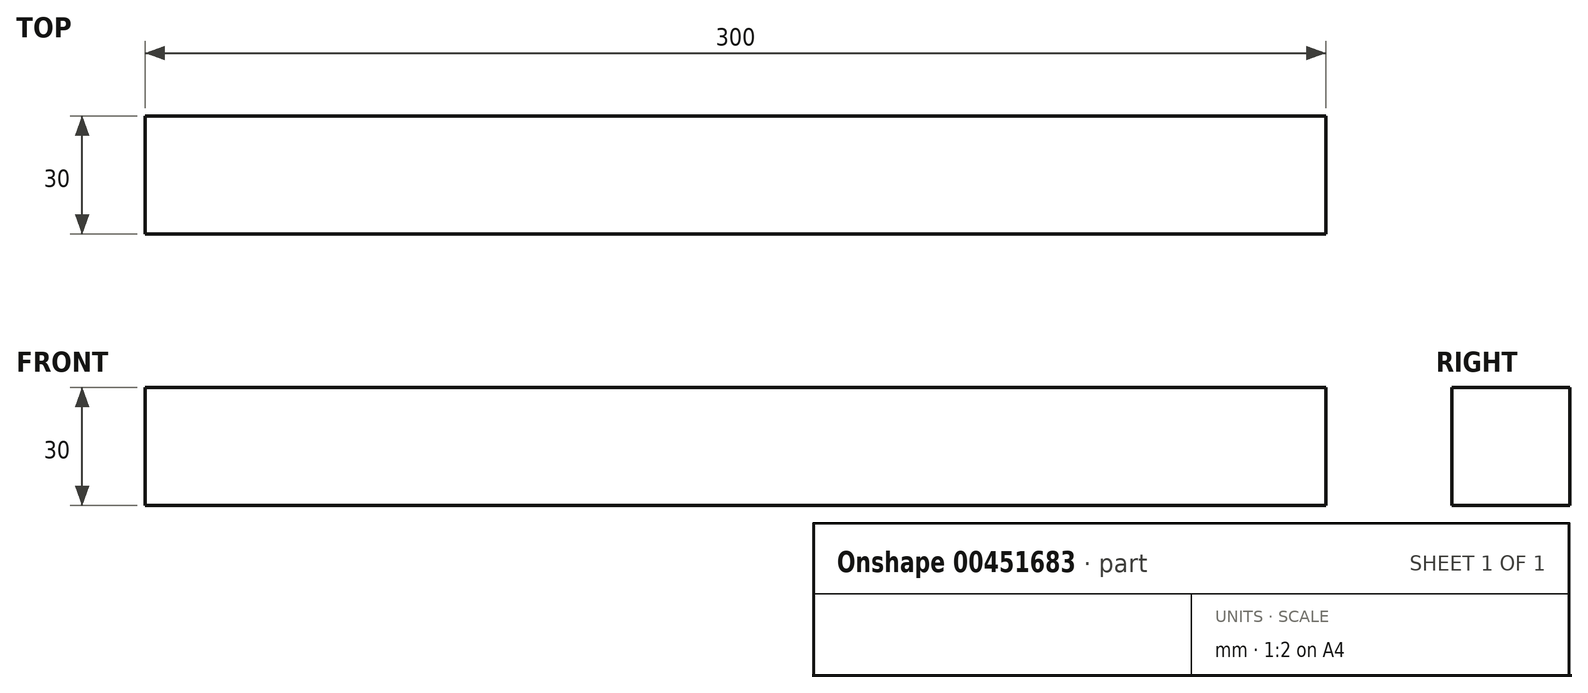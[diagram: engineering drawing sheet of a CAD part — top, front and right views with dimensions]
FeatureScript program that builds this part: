
annotation { "Feature Type Name" : "Feature", "Feature Type Description" : "" }
export const myFeature = defineFeature(function(context is Context, id is Id, definition is map)
    precondition{}
    {
        {
            var Q0;
            Q0=qCreatedBy(makeId("Right.planeOp"),FACE);
            var sketch = newSketch(context, id + "F0", { "sketchPlane" : qUnion([Q0])});
            skLineSegment(sketch, "E0.bottom", {"start": v(0, 0) * mm, "end": v(30, 0) * mm});
            skLineSegment(sketch, "E0.top", {"start": v(0, 30) * mm, "end": v(30, 30) * mm});
            skLineSegment(sketch, "E0.left", {"start": v(0, 0) * mm, "end": v(0, 30) * mm});
            skLineSegment(sketch, "E0.right", {"start": v(30, 0) * mm, "end": v(30, 30) * mm});
            skSolve(sketch);
        }
        {
            var Q0;
            Q0 = qSketchRegion(id + "F0", true);
            extrude(context, id + "F1", {"entities" : qUnion([Q0]), "depth" : 300 * mm});
        }
    });
